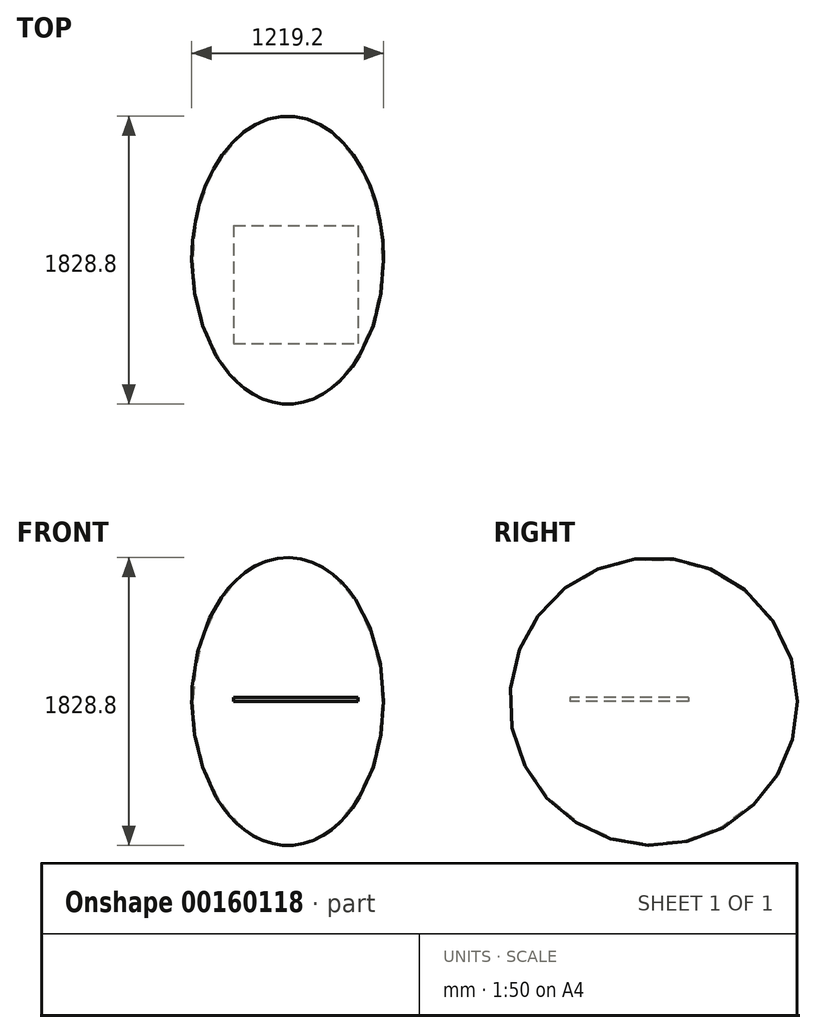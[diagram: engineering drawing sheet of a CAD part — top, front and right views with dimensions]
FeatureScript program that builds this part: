
annotation { "Feature Type Name" : "Feature", "Feature Type Description" : "" }
export const myFeature = defineFeature(function(context is Context, id is Id, definition is map)
    precondition{}
    {
        {
            var Q0;
            Q0=qCreatedBy(makeId("Top.planeOp"),FACE);
            var sketch = newSketch(context, id + "F0", { "sketchPlane" : qUnion([Q0])});
            skLineSegment(sketch, "E0", {"start": v(-609.6, 0) * mm, "end": v(609.6, 0) * mm});
            skEllipticalArc(sketch, "E1", {});
            skLineSegment(sketch, "E2", {"start": v(-779.76, 0) * mm, "end": v(-1001.1, 0) * mm});
            const initialGuessF0  = {"E1": [0, 0, 0, 1, 0.9144, 0.6096, 4.71238898038469, 1.5707963267948966]};
            skSetInitialGuess(sketch, initialGuessF0);
            skSolve(sketch);
        }
        {
            var Q0;
            Q0=makeQuery(id+"F0.imprint","IMPRINT",FACE,{"disambiguationData":[TD([[makeQuery(id+"F0.imprint","IMPRINT",EDGE,{"derivedFrom":sQuery(id+"F0.wireOp",EDGE,"E0")}),1.0]])]});
            var Q1;
            Q1=sQuery(id+"F0.wireOp",EDGE,"E2");
            revolve(context, id + "F1", {"entities" : qUnion([Q0]), "axis" : qUnion([Q1]), "revolveType" : RevolveType.FULL});
        }
        {
            var Q0;
            Q0=makeQuery(id+"F1.opRevolve","SWEPT_FACE",FACE,{"disambiguationData":[OSD([sQuery(id+"F0.wireOp",EDGE,"E1")])]});
            var Q1;
            Q1=makeQuery(id+"F1.opRevolve","SWEPT_BODY",BODY,{"disambiguationData":[OSD([sQuery(id+"F0.wireOp",EDGE,"E0"),sQuery(id+"F0.wireOp",EDGE,"E1")])]});
            shell(context, id + "F2", {"isHollow" : true, "entities" : qUnion([Q0]), "parts" : qUnion([Q1]), "thickness" : 6.35 * mm});
        }
        {
            var Q0;
            Q0=qCreatedBy(makeId("Top.planeOp"),FACE);
            var sketch = newSketch(context, id + "F3", { "sketchPlane" : qUnion([Q0])});
            skLineSegment(sketch, "E3.bottom", {"start": v(-344.49, 219.5) * mm, "end": v(447.1, 219.5) * mm});
            skLineSegment(sketch, "E3.top", {"start": v(-344.49, -531.82) * mm, "end": v(447.1, -531.82) * mm});
            skLineSegment(sketch, "E3.left", {"start": v(-344.49, 219.5) * mm, "end": v(-344.49, -531.82) * mm});
            skLineSegment(sketch, "E3.right", {"start": v(447.1, 219.5) * mm, "end": v(447.1, -531.82) * mm});
            skSolve(sketch);
        }
        {
            var Q0;
            Q0 = qSketchRegion(id + "F3", true);
            extrude(context, id + "F4", {"entities" : qUnion([Q0]), "depth" : 25.4 * mm});
        }
    });
